# Revit family: DBLTD_TheSenatorGroup_LoungeChairs_Aura_Curved
name_source: partatom
category: Furniture
units: mm (PartAtom-declared; Revit-internal decimal feet)

## family parameters
Always vertical = Yes
Cut with Voids When Loaded = No
OmniClass Number = 23.40.20.00
OmniClass Title = General Furniture and Specialties
Render Appearance Source = Family Geometry
Room Calculation Point = No
Shared = Yes
Work Plane-Based = No

## types (24) — shared parameters
Assembly Code = E2020200
AssetType = Movable
Category = Pr_40_50_12_57 Office chairs
Color = Upholstery: Various Options Available
DurationUnit = years
ExpectedLife = 5
Finish = Upholstery: Various Options Available
Keynote = Pr_40_50_12_57 Office chairs
Manufacturer = The Senator Group
ManufacturerName = The Senator Group
ManufacturerURL = https://www.allermuir.com
Material = Cut Foam Seat Carcass | Fully Upholstered | Plastic Glides with Felt
Name = Lounge Sofa
NominalDepth = 965 mm  [stored 3.16601 ft]
ProductInformation = https://www.allermuir.com
SeatingHeight = 420 mm  [stored 1.37795 ft]
Shape = Rectangular
URL = https://www.thesenatorgroup.com
Uniclass2015Code = Pr_40_50_12_48
Uniclass2015Title = Lounge chairs
Uniclass2015Version = Products v1.39
Version = 1
WarrantyDescription = The Senator Group warrants that its manufactured products are free from manufacturing defects - in materials or workmanship - for a period of five (5) years.
WarrantyDurationLabor = 5
WarrantyDurationParts = 5
WarrantyDurationUnit = years
WarrantyGuarantorLabor = https://www.thesenatorgroup.com
WarrantyGuarantorParts = https://www.thesenatorgroup.com
zero-valued in all types: Cost, Default Elevation

## per-type parameters (varying)
| type | Constituents | Description | HasLeftLink | HasRightLink | IsConcaveSingle | IsConcaveTriple | IsConvexSingle | IsConvexTriple | Model | ModelNumber | ModelReference | NominalHeight | NominalWidth | Size | Type Comments | WithBack | WithoutBack |
| Concave 1 Unit with Back and Left Link | Seat and Back | Concave 1 Unit with Back and Left Link | Yes | No | Yes | No | No | No | AURLS11CAVL | AURLS11CAVL | Concave 1 Unit with Back and Left Link | 750 mm  [stored 2.46063 ft] | 330 mm | 750h x 330w x 965d mm | Concave 1 Unit with Back and Left Link | Yes | No |
| Concave 1 Unit with Left Link | Seat | Concave 1 Unit with Left Link | Yes | No | Yes | No | No | No | AURLS01CAVL | AURLS01CAVL | Concave 1 Unit with Left Link | 420 mm  [stored 1.37795 ft] | 330 mm | 420h x 330w x 965d mm | Concave 1 Unit with Left Link | No | Yes |
| Convex 1 Unit with Back and Left Link | Seat and Back | Convex 1 Unit with Back and Left Link | Yes | No | No | No | Yes | No | AURLS11VEXL | AURLS11VEXL | Convex 1 Unit with Back and Left Link | 750 mm  [stored 2.46063 ft] | 330 mm | 750h x 330w x 965d mm | Convex 1 Unit with Back and Left Link | Yes | No |
| Convex 1 Unit with Left Link | Seat | Convex 1 Unit with Left Link | Yes | No | No | No | Yes | No | AURLS01VEXL | AURLS01VEXL | Convex 1 Unit with Left Link | 420 mm  [stored 1.37795 ft] | 330 mm | 420h x 330w x 965d mm | Convex 1 Unit with Left Link | No | Yes |
| Concave 3 Units with Back and Left Link | Seat and Back | Concave 3 Units with Back and Left Link | Yes | No | Yes | Yes | No | No | AURLS13CAVL | AURLS13CAVL | Concave 3 Units with Back and Left Link | 750 mm  [stored 2.46063 ft] | 990 mm  [stored 3.24803 ft] | 750h x 990w x 965d mm | Concave 3 Units with Back and Left Link | Yes | No |
| Concave 3 Units with Left Link | Seat | Concave 3 Units with Left Link | Yes | No | Yes | Yes | No | No | AURLS03CAVL | AURLS03CAVL | Concave 3 Units with Left Link | 420 mm  [stored 1.37795 ft] | 990 mm  [stored 3.24803 ft] | 420h x 990w x 965d mm | Concave 3 Units with Left Link | No | Yes |
| Convex 3 Units with Back and Left Link | Seat and Back | Convex 3 Units with Back and Left Link | Yes | No | No | No | Yes | Yes | AURLS13VEXL | AURLS13VEXL | Convex 3 Units with Back and Left Link | 750 mm  [stored 2.46063 ft] | 990 mm  [stored 3.24803 ft] | 750h x 990w x 965d mm | Convex 3 Units with Back and Left Link | Yes | No |
| Convex 3 Units with Left Link | Seat | Convex 3 Units with Left Link | Yes | No | No | No | Yes | Yes | AURLS03VEXL | AURLS03VEXL | Convex 3 Units with Left Link | 420 mm  [stored 1.37795 ft] | 990 mm  [stored 3.24803 ft] | 420h x 990w x 965d mm | Convex 3 Units with Left Link | No | Yes |
| Concave 1 Unit with Back and Right Link | Seat and Back | Concave 1 Unit with Back and Right Link | No | Yes | Yes | No | No | No | AURLS11CAVR | AURLS11CAVR | Concave 1 Unit with Back and Right Link | 750 mm  [stored 2.46063 ft] | 330 mm | 750h x 330w x 965d mm | Concave 1 Unit with Back and Right Link | Yes | No |
| Concave 1 Unit with Right Link | Seat | Concave 1 Unit with Right Link | No | Yes | Yes | No | No | No | AURLS01CAVR | AURLS01CAVR | Concave 1 Unit with Right Link | 420 mm  [stored 1.37795 ft] | 330 mm | 420h x 330w x 965d mm | Concave 1 Unit with Right Link | No | Yes |
| Convex 1 Unit with Back and Right Link | Seat and Back | Convex 1 Unit with Back and Right Link | No | Yes | No | No | Yes | No | AURLS11VEXR | AURLS11VEXR | Convex 1 Unit with Back and Right Link | 750 mm  [stored 2.46063 ft] | 330 mm | 750h x 330w x 965d mm | Convex 1 Unit with Back and Right Link | Yes | No |
| Convex 1 Unit with Right Link | Seat | Convex 1 Unit with Right Link | No | Yes | No | No | Yes | No | AURLS01VEXR | AURLS01VEXR | Convex 1 Unit with Right Link | 420 mm  [stored 1.37795 ft] | 330 mm | 420h x 330w x 965d mm | Convex 1 Unit with Right Link | No | Yes |
| Concave 3 Units with Back and Right Link | Seat and Back | Concave 3 Units with Back and Right Link | No | Yes | Yes | Yes | No | No | AURLS13CAVR | AURLS13CAVR | Concave 3 Units with Back and Right Link | 750 mm  [stored 2.46063 ft] | 990 mm  [stored 3.24803 ft] | 750h x 990w x 965d mm | Concave 3 Units with Back and Right Link | Yes | No |
| Concave 3 Units with Right Link | Seat | Concave 3 Units with Right Link | No | Yes | Yes | Yes | No | No | AURLS03CAVR | AURLS03CAVR | Concave 3 Units with Right Link | 420 mm  [stored 1.37795 ft] | 990 mm  [stored 3.24803 ft] | 420h x 990w x 965d mm | Concave 3 Units with Right Link | No | Yes |
| Convex 3 Units with Back and Right Link | Seat and Back | Convex 3 Units with Back and Right Link | No | Yes | No | No | Yes | Yes | AURLS13VEXR | AURLS13VEXR | Convex 3 Units with Back and Right Link | 750 mm  [stored 2.46063 ft] | 990 mm  [stored 3.24803 ft] | 750h x 990w x 965d mm | Convex 3 Units with Back and Right Link | Yes | No |
| Convex 3 Units with Right Link | Seat | Convex 3 Units with Right Link | No | Yes | No | No | Yes | Yes | AURLS03VEXR | AURLS03VEXR | Convex 3 Units with Right Link | 420 mm  [stored 1.37795 ft] | 990 mm  [stored 3.24803 ft] | 420h x 990w x 965d mm | Convex 3 Units with Right Link | No | Yes |
| Concave 1 Unit with Back and Both Links | Seat and Back | Concave 1 Unit with Back and Right Link | Yes | Yes | Yes | No | No | No | AURLS11CAVM | AURLS11CAVM | Concave 1 Unit with Back and Right Link | 750 mm  [stored 2.46063 ft] | 330 mm | 750h x 330w x 965d mm | Concave 1 Unit with Back and Right Link | Yes | No |
| Concave 1 Unit with Both Links | Seat | Concave 1 Unit with Right Link | Yes | Yes | Yes | No | No | No | AURLS01CAVM | AURLS01CAVM | Concave 1 Unit with Right Link | 420 mm  [stored 1.37795 ft] | 330 mm | 420h x 330w x 965d mm | Concave 1 Unit with Right Link | No | Yes |
| Convex 1 Unit with Back and Both Links | Seat and Back | Convex 1 Unit with Back and Right Link | Yes | Yes | No | No | Yes | No | AURLS11VEXM | AURLS11VEXM | Convex 1 Unit with Back and Right Link | 750 mm  [stored 2.46063 ft] | 330 mm | 750h x 330w x 965d mm | Convex 1 Unit with Back and Right Link | Yes | No |
| Convex 1 Unit with Both Links | Seat | Convex 1 Unit with Right Link | Yes | Yes | No | No | Yes | No | AURLS01VEXM | AURLS01VEXM | Convex 1 Unit with Right Link | 420 mm  [stored 1.37795 ft] | 330 mm | 420h x 330w x 965d mm | Convex 1 Unit with Right Link | No | Yes |
| Concave 3 Units with Back and Both Links | Seat and Back | Concave 3 Units with Back and Right Link | Yes | Yes | Yes | Yes | No | No | AURLS13CAVM | AURLS13CAVM | Concave 3 Units with Back and Right Link | 750 mm  [stored 2.46063 ft] | 990 mm  [stored 3.24803 ft] | 750h x 990w x 965d mm | Concave 3 Units with Back and Right Link | Yes | No |
| Concave 3 Units with Both Links | Seat | Concave 3 Units with Right Link | Yes | Yes | Yes | Yes | No | No | AURLS03CAVM | AURLS03CAVM | Concave 3 Units with Right Link | 420 mm  [stored 1.37795 ft] | 990 mm  [stored 3.24803 ft] | 420h x 990w x 965d mm | Concave 3 Units with Right Link | No | Yes |
| Convex 3 Units with Back and Both Links | Seat and Back | Convex 3 Units with Back and Right Link | Yes | Yes | No | No | Yes | Yes | AURLS13VEXM | AURLS13VEXM | Convex 3 Units with Back and Right Link | 750 mm  [stored 2.46063 ft] | 990 mm  [stored 3.24803 ft] | 750h x 990w x 965d mm | Convex 3 Units with Back and Right Link | Yes | No |
| Convex 3 Units with Both Links | Seat | Convex 3 Units with Right Link | Yes | Yes | No | No | Yes | Yes | AURLS03VEXM | AURLS03VEXM | Convex 3 Units with Right Link | 420 mm  [stored 1.37795 ft] | 990 mm  [stored 3.24803 ft] | 420h x 990w x 965d mm | Convex 3 Units with Right Link | No | Yes |

note: [stored X ft] marks values corroborated as IEEE doubles in the binary element streams (Revit-internal decimal feet)

## geometry (parser evidence)
native form markers: Sweep x6
no freeform markers — native parametric forms only
